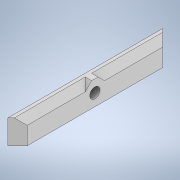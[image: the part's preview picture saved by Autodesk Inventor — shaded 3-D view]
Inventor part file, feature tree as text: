
AUTODESK INVENTOR PART (.ipt)
format: ipt  version: 2021 (Build 250183000, 183)  size: 143,360 bytes
history: native  units: in
note: dims shown in document units (in); Inventor stores cm internally (conversion verified against a paired STEP export)
features: extrude x4, sketch x4, projected_geometry x1
ambient origin geometry x8: Origin, YZ Plane, XZ Plane, XY Plane, X Axis, Y Axis, Z Axis, Center Point
bodies: Solid1 (feature_tree)
feature tree (9):
  extrude  "Extrusion1"  Depth=0.2362in
  extrude  "Extrusion2"  Depth=0.5906in
  extrude  "Extrusion3"  Depth=0.2362in
  extrude  "Extrusion4"  Depth=0.3937in TaperAngle=0.0deg
  sketch  "Sketch1"  dims[d0=0.2362in d1=0.4331in]
  sketch  "Sketch2"  dims[d2=0.5906in d3=0.0787in]
  sketch  "Sketch3"  dims[d4=3.7795in d5=0.0in d7=0.2362in]
  sketch  "Sketch4"  dims[d8=0.2362in d9=1.658in d10=0.0in d11=0.2362in d12=0.2362in d13=0.0787in d14=0.0787in d15=0.2362in d16=0.0in d17=0.2953in d18=0.252in d19=0.3937in d20=0.0in]
  projected_geometry  "Projected Loop1"
